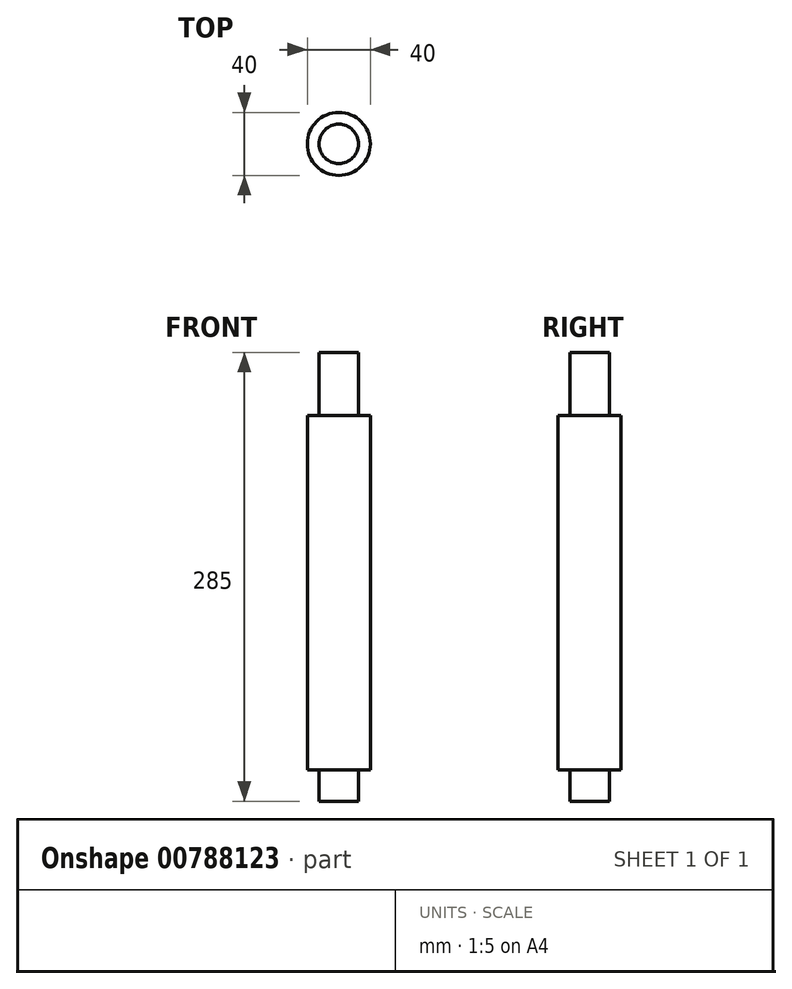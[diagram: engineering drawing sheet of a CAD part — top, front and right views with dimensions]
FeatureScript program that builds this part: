
annotation { "Feature Type Name" : "Feature", "Feature Type Description" : "" }
export const myFeature = defineFeature(function(context is Context, id is Id, definition is map)
    precondition{}
    {
        {
            var Q0;
            Q0=qCreatedBy(makeId("Front.planeOp"),FACE);
            var sketch = newSketch(context, id + "F0", { "sketchPlane" : qUnion([Q0])});
            skLineSegment(sketch, "E0", {"start": v(0, -20) * mm, "end": v(-12.5, -20) * mm});
            skLineSegment(sketch, "E1", {"start": v(-12.5, -20) * mm, "end": v(-12.5, 0) * mm});
            skLineSegment(sketch, "E2", {"start": v(-12.5, 0) * mm, "end": v(-20, 0) * mm});
            skLineSegment(sketch, "E3", {"start": v(-20, 0) * mm, "end": v(-20, 225) * mm});
            skLineSegment(sketch, "E4", {"start": v(-20, 225) * mm, "end": v(-12.5, 225) * mm});
            skLineSegment(sketch, "E5", {"start": v(-12.5, 225) * mm, "end": v(-12.5, 265) * mm});
            skLineSegment(sketch, "E6", {"start": v(-12.5, 265) * mm, "end": v(0, 265) * mm});
            skLineSegment(sketch, "E7", {"start": v(0, 265) * mm, "end": v(0, -20) * mm});
            skLineSegment(sketch, "E8", {"start": v(0, -86.38) * mm, "end": v(0, 245.22) * mm, "construction": true});
            skSolve(sketch);
        }
        {
            var Q0;
            Q0 = qSketchRegion(id + "F0", true);
            var Q1;
            Q1=sQuery(id+"F0.wireOp",EDGE,"E8");
            revolve(context, id + "F1", {"surfaceOperationType" : NewSurfaceOperationType.NEW, "entities" : qUnion([Q0]), "axis" : qUnion([Q1]), "revolveType" : RevolveType.FULL});
        }
    });
